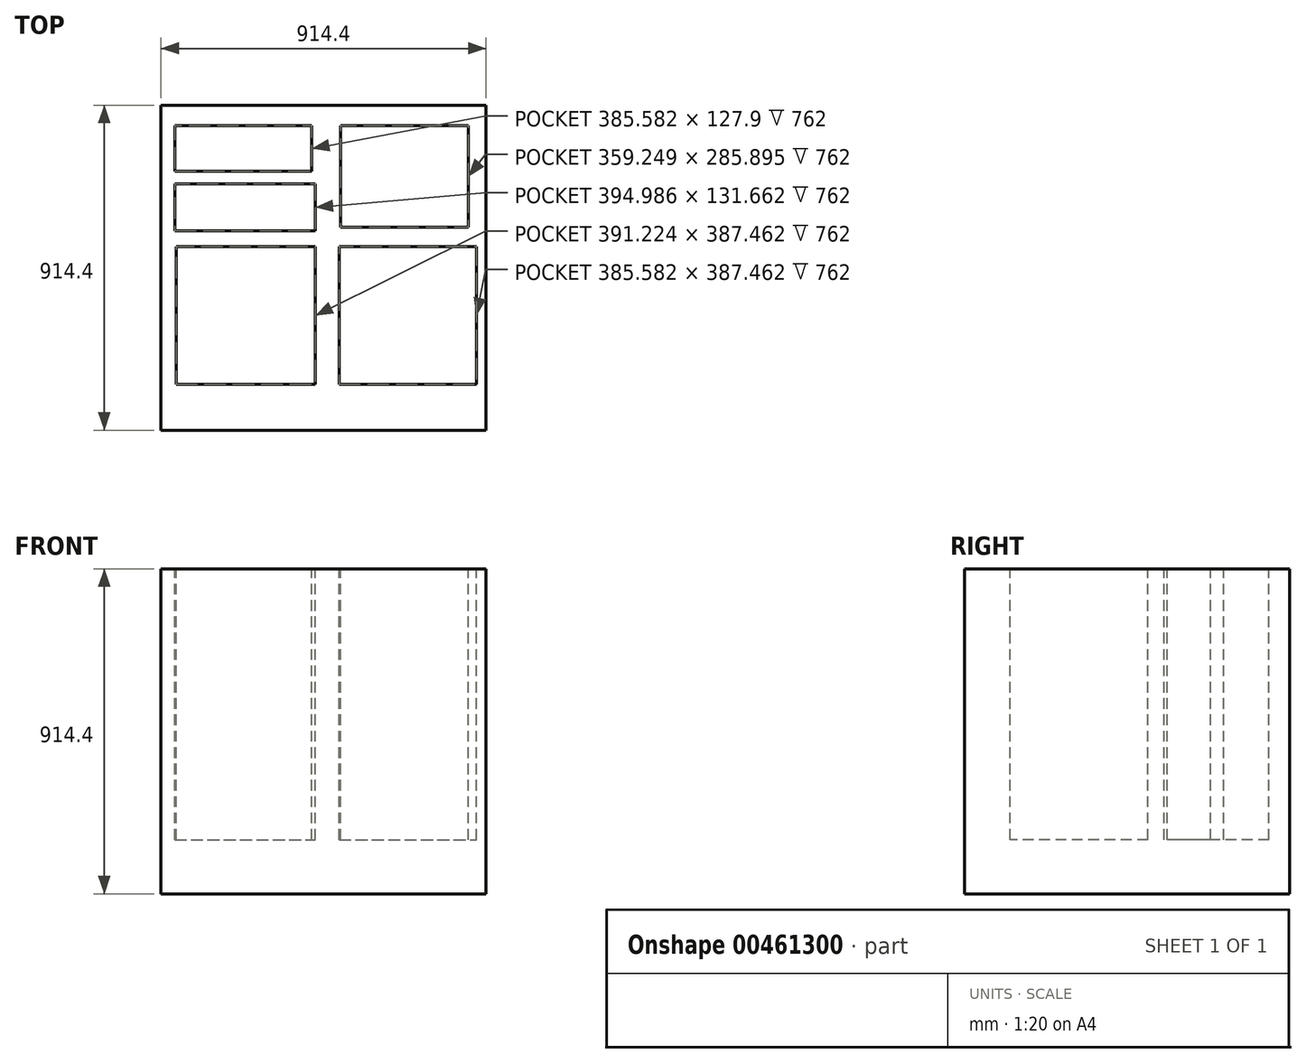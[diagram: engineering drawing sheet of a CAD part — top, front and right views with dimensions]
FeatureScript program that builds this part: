
annotation { "Feature Type Name" : "Feature", "Feature Type Description" : "" }
export const myFeature = defineFeature(function(context is Context, id is Id, definition is map)
    precondition{}
    {
        {
            var Q0;
            Q0=qCreatedBy(makeId("Top.planeOp"),FACE);
            var sketch = newSketch(context, id + "F0", { "sketchPlane" : qUnion([Q0])});
            skLineSegment(sketch, "E0.bottom", {"start": v(0, 0) * mm, "end": v(-914.4, 0) * mm});
            skLineSegment(sketch, "E0.top", {"start": v(0, 914.4) * mm, "end": v(-914.4, 914.4) * mm});
            skLineSegment(sketch, "E0.left", {"start": v(0, 0) * mm, "end": v(0, 914.4) * mm});
            skLineSegment(sketch, "E0.right", {"start": v(-914.4, 0) * mm, "end": v(-914.4, 914.4) * mm});
            skSolve(sketch);
        }
        {
            var Q0;
            Q0=makeQuery(id+"F0.imprint","IMPRINT",FACE,{"disambiguationData":[TD([[makeQuery(id+"F0.imprint","IMPRINT",EDGE,{"derivedFrom":sQuery(id+"F0.wireOp",EDGE,"E0.bottom")}),-1.0]])]});
            extrude(context, id + "F1", {"entities" : qUnion([Q0]), "depth" : 914.4 * mm});
        }
        {
            var Q0;
            Q0=makeQuery(id+"F1.opExtrude","CAP_FACE",FACE,{"disambiguationData":[OSD([sQuery(id+"F0.wireOp",EDGE,"E0.bottom"),sQuery(id+"F0.wireOp",EDGE,"E0.top"),sQuery(id+"F0.wireOp",EDGE,"E0.left"),sQuery(id+"F0.wireOp",EDGE,"E0.right")])],"isStart":false});
            var sketch = newSketch(context, id + "F2", { "sketchPlane" : qUnion([Q0])});
            skLineSegment(sketch, "E1.bottom", {"start": v(-876.16, 856.4) * mm, "end": v(-490.57, 856.4) * mm});
            skLineSegment(sketch, "E1.top", {"start": v(-876.16, 728.5) * mm, "end": v(-490.57, 728.5) * mm});
            skLineSegment(sketch, "E1.left", {"start": v(-876.16, 856.4) * mm, "end": v(-876.16, 728.5) * mm});
            skLineSegment(sketch, "E1.right", {"start": v(-490.57, 856.4) * mm, "end": v(-490.57, 728.5) * mm});
            skLineSegment(sketch, "E2.bottom", {"start": v(-876.16, 692.77) * mm, "end": v(-481.17, 692.77) * mm});
            skLineSegment(sketch, "E2.top", {"start": v(-876.16, 561.1) * mm, "end": v(-481.17, 561.1) * mm});
            skLineSegment(sketch, "E2.left", {"start": v(-876.16, 692.77) * mm, "end": v(-876.16, 561.1) * mm});
            skLineSegment(sketch, "E2.right", {"start": v(-481.17, 692.77) * mm, "end": v(-481.17, 561.1) * mm});
            skLineSegment(sketch, "E3.bottom", {"start": v(-872.4, 515.97) * mm, "end": v(-481.17, 515.97) * mm});
            skLineSegment(sketch, "E3.top", {"start": v(-872.4, 128.5) * mm, "end": v(-481.17, 128.5) * mm});
            skLineSegment(sketch, "E3.left", {"start": v(-872.4, 515.97) * mm, "end": v(-872.4, 128.5) * mm});
            skLineSegment(sketch, "E3.right", {"start": v(-481.17, 515.97) * mm, "end": v(-481.17, 128.5) * mm});
            skLineSegment(sketch, "E4.bottom", {"start": v(-413.46, 515.97) * mm, "end": v(-27.88, 515.97) * mm});
            skLineSegment(sketch, "E4.top", {"start": v(-413.46, 128.5) * mm, "end": v(-27.88, 128.5) * mm});
            skLineSegment(sketch, "E4.left", {"start": v(-413.46, 515.97) * mm, "end": v(-413.46, 128.5) * mm});
            skLineSegment(sketch, "E4.right", {"start": v(-27.88, 515.97) * mm, "end": v(-27.88, 128.5) * mm});
            skLineSegment(sketch, "E5.bottom", {"start": v(-409.7, 856.4) * mm, "end": v(-50.45, 856.4) * mm});
            skLineSegment(sketch, "E5.top", {"start": v(-409.7, 570.51) * mm, "end": v(-50.45, 570.51) * mm});
            skLineSegment(sketch, "E5.left", {"start": v(-409.7, 856.4) * mm, "end": v(-409.7, 570.51) * mm});
            skLineSegment(sketch, "E5.right", {"start": v(-50.45, 856.4) * mm, "end": v(-50.45, 570.51) * mm});
            skSolve(sketch);
        }
        {
            var Q0;
            Q0=makeQuery(id+"F2.imprint","IMPRINT",FACE,{"disambiguationData":[TD([[makeQuery(id+"F2.imprint","IMPRINT",EDGE,{"derivedFrom":sQuery(id+"F2.wireOp",EDGE,"E1.bottom")}),-1.0]])]});
            var Q1;
            Q1=makeQuery(id+"F2.imprint","IMPRINT",FACE,{"disambiguationData":[TD([[makeQuery(id+"F2.imprint","IMPRINT",EDGE,{"derivedFrom":sQuery(id+"F2.wireOp",EDGE,"E5.bottom")}),-1.0]])]});
            var Q2;
            Q2=makeQuery(id+"F2.imprint","IMPRINT",FACE,{"disambiguationData":[TD([[makeQuery(id+"F2.imprint","IMPRINT",EDGE,{"derivedFrom":sQuery(id+"F2.wireOp",EDGE,"E2.bottom")}),-1.0]])]});
            var Q3;
            Q3=makeQuery(id+"F2.imprint","IMPRINT",FACE,{"disambiguationData":[TD([[makeQuery(id+"F2.imprint","IMPRINT",EDGE,{"derivedFrom":sQuery(id+"F2.wireOp",EDGE,"E3.bottom")}),-1.0]])]});
            var Q4;
            Q4=makeQuery(id+"F2.imprint","IMPRINT",FACE,{"disambiguationData":[TD([[makeQuery(id+"F2.imprint","IMPRINT",EDGE,{"derivedFrom":sQuery(id+"F2.wireOp",EDGE,"E4.bottom")}),-1.0]])]});
            extrude(context, id + "F3", {"entities" : qUnion([Q0, Q1, Q2, Q3, Q4]), "operationType" : NewBodyOperationType.REMOVE, "depth" : -762 * mm});
        }
    });
